# Revit family: Tomas sin enclavamiento 250 V
name_source: partatom
category: Installations électriques
revit_build: Autodesk Revit 2018 (Build: 20170223_1515(x64)
units: mm (PartAtom-declared; Revit-internal decimal feet)

## family parameters
Conserver l'orientation des annotations = Non
Cote de connecteur circulaire = Utiliser le diamètre
Couper avec des vides une fois chargée = Non
Hôte = Face
Partagée = Non
Point de calcul de pièce = Non
Type d'élément = Normal

## types (9) — shared parameters
Elévation par défaut = 1000 mm  [stored 3.28084 ft]
Fabricant = Legrand
Familia produce = 0854-P17 TEMPRA PRO
Temperatura maxima de uso = 40
Temperatura minima de uso = -25
Toma estándar internacional para montaje empotrado o montaje en superficie con accesorio permite la conexión de dispositivos de alimentación = Toma para uso doméstico
clase de protección IP = IP54
instalación de empotrar E o de superficie S = empotrar
intensidad A = 16 A
materia de la caja = plástico
profundidad de empotrar mm = 26 mm
profundidad mm = 43 mm  [stored 0.141076 ft]
resistencia a los choques IK = 8
sin halogeno = Oui
tipo de conexión = conexión por tonillo
zero-valued in all types: posición de la tierra h

## per-type parameters (varying)
| type | Description | Estándar CEI o NFC | Tension V | altura mm | ancho mm | color característico | distancia de fijación horizontal mm | distancia de fijación vertical mm | numero de polos |
| LG-057676 - P17 - 250 V - 16 A - 2P+T | LG-057676_Panel de montaje toma P17  250 V - 16 A - 2P+T | SCHUKO |  | 75 mm | 75 mm | azul | 60 mm | 60 mm | 2 |
| LG-057675 - P17 - 250 V - 16 A - 2P+T | LG-057675_Panel de montaje toma P17 I- 250 V - 16 A - 2P+T | SCHUKO |  | 62 mm | 50 mm  [stored 0.164042 ft] | blanco | 38 mm | 38 mm | 2 |
| LG-057674 - P17 - IP54 - 250 V - 16 A - 2P+T | LG-057674_Toma P17 - IP54 - 250 V - 16 A - 2P+T | SCHUKO |  | 62 mm | 50 mm  [stored 0.164042 ft] | blanco | 38 mm | 38 mm | 2 |
| LG-057673 - P17 - IP54 - 250 V - 16 A - 2P+T | LG-057673_Toma P17 - IP54 - 250 V - 16 A - 2P+T | SCHUKO |  | 62 mm | 50 mm  [stored 0.164042 ft] | negro | 38 mm | 38 mm | 2 |
| LG-057672 - P17 - 250 V - 16 A - 2P+T | LG-057672_Panel de montaje toma P17  250 V - 16 A - 2P+T | SCHUKO | 230 V  50/60 Hz azul | 75 mm | 75 mm | azul | 60 mm | 60 mm | 3 |
| LG-057671 - P17 - IP54 - 250 V - 16 A - 2P+T | LG-057671_Toma P17 - IP54 - 250 V - 16 A - 2P+T | SCHUKO | 230 V  50/60 Hz azul | 75 mm | 75 mm | azul | 60 mm | 60 mm | 3 |
| LG-057670 - P17 - IP54 - 250 V - 16 A - 2P+T | LG-057670_Toma P17 IP54 - 250 V - 16 A - 2P+T | SCHUKO | 230 V  50/60 Hz azul | 50 mm  [stored 0.164042 ft] | 50 mm  [stored 0.164042 ft] | azul | 38 mm | 38 mm | 3 |
| LG-057669 - P17 - 250 V - 16 A - 2P+T | LG-057669_Panel de montaje toma P17 - 250 V - 16 A - 2P+T | SCHUKO | 230 V  50/60 Hz azul | 50 mm  [stored 0.164042 ft] | 50 mm  [stored 0.164042 ft] | blanco | 38 mm | 38 mm | 3 |
| LG-057667 - P17 - IP54 - 250 V - 16 A - 2P+T | LG-057667_Toma P17 - IP54 - 250 V - 16 A - 2P+T | NFC | 230 V  50/60 Hz azul | 50 mm  [stored 0.164042 ft] | 50 mm  [stored 0.164042 ft] | azul | 38 mm | 38 mm | 3 |

note: [stored X ft] marks values corroborated as IEEE doubles in the binary element streams (Revit-internal decimal feet)
